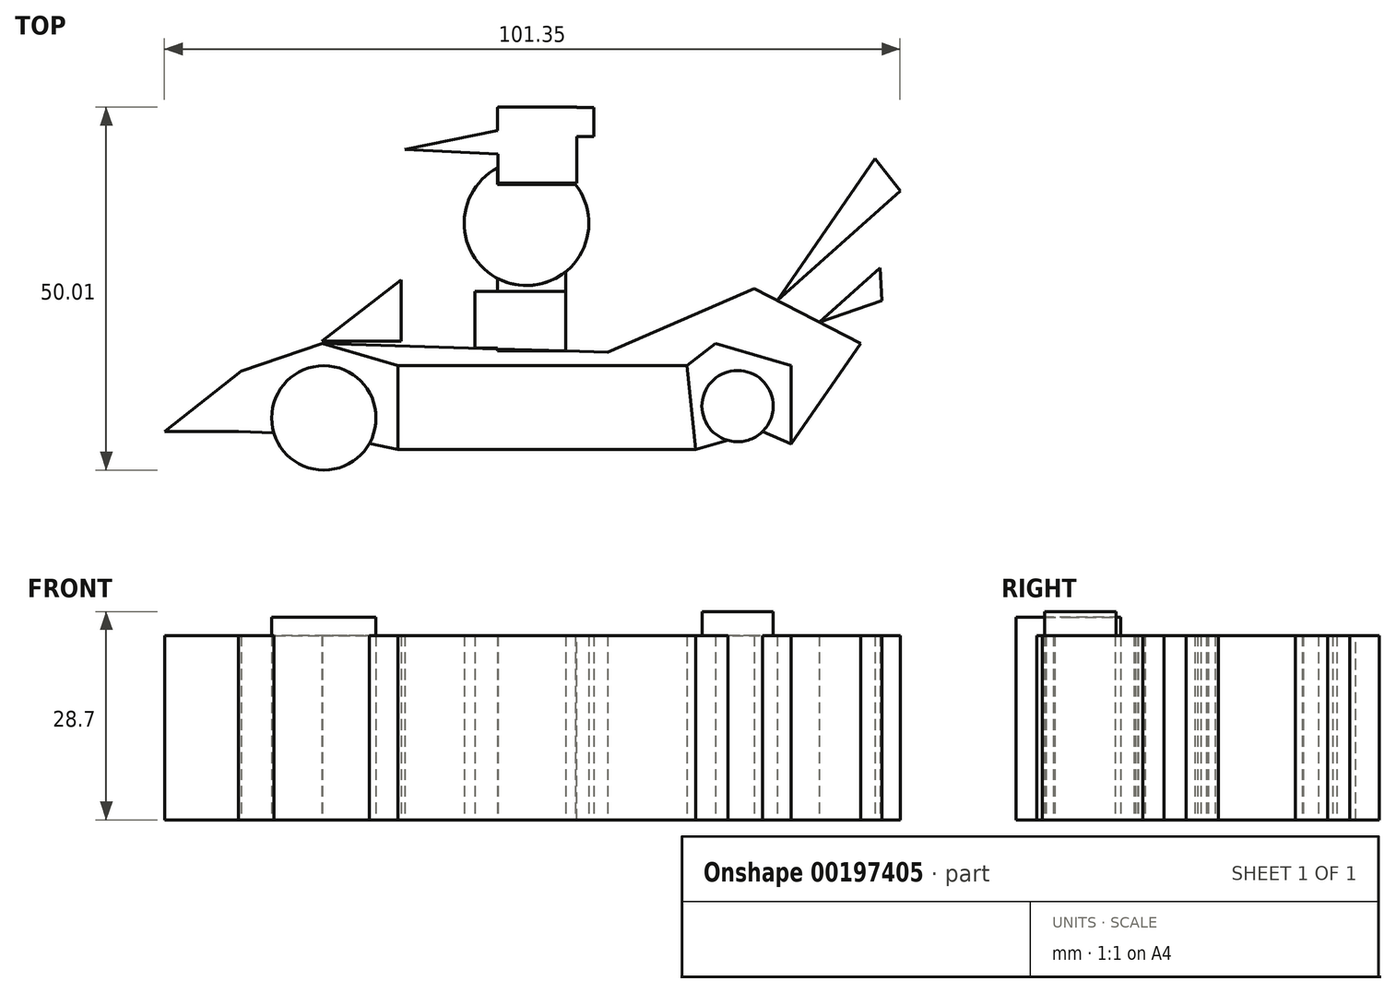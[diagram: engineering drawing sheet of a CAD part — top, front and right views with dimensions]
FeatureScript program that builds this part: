
annotation { "Feature Type Name" : "Feature", "Feature Type Description" : "" }
export const myFeature = defineFeature(function(context is Context, id is Id, definition is map)
    precondition{}
    {
        {
            var Q0;
            Q0=qCreatedBy(makeId("Top.planeOp"),FACE);
            var sketch = newSketch(context, id + "F0", { "sketchPlane" : qUnion([Q0])});
            skLineSegment(sketch, "E0", {"start": v(-28.9, 7.2) * mm, "end": v(10.95, 7.2) * mm});
            skLineSegment(sketch, "E1", {"start": v(-28.9, 7.2) * mm, "end": v(-28.9, -4.36) * mm});
            skLineSegment(sketch, "E2", {"start": v(-28.9, -4.36) * mm, "end": v(12.13, -4.36) * mm});
            skCircle(sketch, "E3", {"center": v(-39.1, 0) * mm, "radius": 7.2 * mm});
            skLineSegment(sketch, "E4", {"start": v(12.13, -4.36) * mm, "end": v(10.95, 7.2) * mm});
            skCircle(sketch, "E5", {"center": v(17.9, 1.63) * mm, "radius": 4.9 * mm});
            skLineSegment(sketch, "E6", {"start": v(-50.45, 6.42) * mm, "end": v(-61.05, -1.86) * mm});
            skLineSegment(sketch, "E7", {"start": v(-61.05, -1.86) * mm, "end": v(-50.84, -1.86) * mm});
            skLineSegment(sketch, "E8", {"start": v(-50.84, -1.86) * mm, "end": v(-50.45, 6.42) * mm});
            skLineSegment(sketch, "E9", {"start": v(-50.45, 6.42) * mm, "end": v(-39.29, 10.27) * mm});
            skLineSegment(sketch, "E10", {"start": v(-39.29, 10.27) * mm, "end": v(-28.9, 7.2) * mm});
            skLineSegment(sketch, "E11", {"start": v(10.95, 7.2) * mm, "end": v(14.89, 10.27) * mm});
            skLineSegment(sketch, "E12", {"start": v(14.89, 10.27) * mm, "end": v(25.28, 7.2) * mm});
            skLineSegment(sketch, "E13", {"start": v(25.28, 7.2) * mm, "end": v(25.28, -3.57) * mm});
            skLineSegment(sketch, "E14", {"start": v(25.28, -3.57) * mm, "end": v(34.85, 10.27) * mm});
            skLineSegment(sketch, "E15", {"start": v(34.85, 10.27) * mm, "end": v(20.22, 17.8) * mm});
            skLineSegment(sketch, "E16", {"start": v(23.35, 16.19) * mm, "end": v(36.85, 35.7) * mm});
            skLineSegment(sketch, "E17", {"start": v(36.85, 35.7) * mm, "end": v(40.3, 31.28) * mm});
            skLineSegment(sketch, "E18", {"start": v(40.3, 31.28) * mm, "end": v(23.35, 16.19) * mm});
            skLineSegment(sketch, "E19", {"start": v(20.22, 17.8) * mm, "end": v(0, 9.06) * mm});
            skLineSegment(sketch, "E20", {"start": v(0, 9.06) * mm, "end": v(-39.29, 10.27) * mm});
            skLineSegment(sketch, "E21", {"start": v(-39.29, 10.27) * mm, "end": v(-28.9, 19.52) * mm});
            skLineSegment(sketch, "E22", {"start": v(-28.9, 19.52) * mm, "end": v(-28.9, 10.27) * mm});
            skLineSegment(sketch, "E23", {"start": v(29.17, 13.2) * mm, "end": v(37.8, 20.88) * mm});
            skLineSegment(sketch, "E24", {"start": v(37.55, 20.88) * mm, "end": v(37.8, 16.19) * mm});
            skCircle(sketch, "E25", {"center": v(-11.17, 26.84) * mm, "radius": 8.59 * mm});
            skLineSegment(sketch, "E26.bottom", {"start": v(-15.38, 36.44) * mm, "end": v(-27.49, 36.44) * mm});
            skLineSegment(sketch, "E26.top", {"start": v(-15.38, 36.05) * mm, "end": v(-27.49, 36.05) * mm});
            skLineSegment(sketch, "E26.left", {"start": v(-15.38, 36.44) * mm, "end": v(-15.38, 36.05) * mm});
            skLineSegment(sketch, "E26.right", {"start": v(-27.49, 36.44) * mm, "end": v(-27.49, 36.05) * mm});
            skLineSegment(sketch, "E27.bottom", {"start": v(-27.49, 36.44) * mm, "end": v(-15.17, 36.44) * mm});
            skLineSegment(sketch, "E27.top", {"start": v(-27.49, 38.75) * mm, "end": v(-15.17, 38.75) * mm});
            skLineSegment(sketch, "E27.left", {"start": v(-27.49, 36.44) * mm, "end": v(-27.49, 38.75) * mm});
            skLineSegment(sketch, "E27.right", {"start": v(-15.17, 36.44) * mm, "end": v(-15.17, 38.75) * mm});
            skLineSegment(sketch, "E28.bottom", {"start": v(-15.17, 38.75) * mm, "end": v(-1.92, 38.75) * mm});
            skLineSegment(sketch, "E28.top", {"start": v(-15.17, 42.79) * mm, "end": v(-1.92, 42.79) * mm});
            skLineSegment(sketch, "E28.left", {"start": v(-15.17, 38.75) * mm, "end": v(-15.17, 42.79) * mm});
            skLineSegment(sketch, "E28.right", {"start": v(-1.92, 38.75) * mm, "end": v(-1.92, 42.79) * mm});
            skLineSegment(sketch, "E29.bottom", {"start": v(-15.17, 36.44) * mm, "end": v(-1.92, 36.44) * mm});
            skLineSegment(sketch, "E29.right", {"start": v(-1.92, 36.44) * mm, "end": v(-1.92, 38.75) * mm});
            skPoint(sketch, "E30.firstSnap0", {"position": v(-15.17, 40.77) * mm});
            skLineSegment(sketch, "E30.bottom", {"start": v(-15.17, 17.41) * mm, "end": v(-18.27, 17.41) * mm});
            skLineSegment(sketch, "E30.top", {"start": v(-15.17, 9.62) * mm, "end": v(-18.27, 9.62) * mm});
            skLineSegment(sketch, "E30.left", {"start": v(-15.17, 17.41) * mm, "end": v(-15.17, 9.62) * mm});
            skLineSegment(sketch, "E30.right", {"start": v(-18.27, 17.41) * mm, "end": v(-18.27, 9.62) * mm});
            skLineSegment(sketch, "E31.bottom", {"start": v(-15.17, 17.41) * mm, "end": v(-5.74, 17.41) * mm});
            skLineSegment(sketch, "E31.top", {"start": v(-15.17, 9.24) * mm, "end": v(-5.74, 9.24) * mm});
            skLineSegment(sketch, "E31.left", {"start": v(-15.17, 17.41) * mm, "end": v(-15.17, 9.24) * mm});
            skLineSegment(sketch, "E31.right", {"start": v(-5.74, 17.41) * mm, "end": v(-5.74, 9.24) * mm});
            skLineSegment(sketch, "E32.top", {"start": v(-15.17, 20.18) * mm, "end": v(-5.74, 20.18) * mm});
            skLineSegment(sketch, "E32.left", {"start": v(-15.17, 17.41) * mm, "end": v(-15.17, 20.18) * mm});
            skLineSegment(sketch, "E32.right", {"start": v(-5.74, 17.41) * mm, "end": v(-5.74, 20.18) * mm});
            skLineSegment(sketch, "E33.bottom", {"start": v(-15.17, 36.44) * mm, "end": v(-4.46, 36.44) * mm});
            skLineSegment(sketch, "E33.top", {"start": v(-15.17, 32.2) * mm, "end": v(-4.46, 32.2) * mm});
            skLineSegment(sketch, "E33.left", {"start": v(-15.17, 36.44) * mm, "end": v(-15.17, 32.2) * mm});
            skLineSegment(sketch, "E33.right", {"start": v(-4.46, 36.44) * mm, "end": v(-4.46, 32.2) * mm});
            skLineSegment(sketch, "E34", {"start": v(-50.84, -1.86) * mm, "end": v(-45.97, -2.1) * mm});
            skLineSegment(sketch, "E35", {"start": v(-32.8, -3.5) * mm, "end": v(-28.9, -4.36) * mm});
            skLineSegment(sketch, "E36", {"start": v(12.13, -4.36) * mm, "end": v(16.55, -3.1) * mm});
            skLineSegment(sketch, "E37", {"start": v(21.36, -1.86) * mm, "end": v(25.28, -3.57) * mm});
            skLineSegment(sketch, "E38", {"start": v(29.17, 13.2) * mm, "end": v(37.8, 16.19) * mm});
            skSolve(sketch);
        }
        {
            var Q0;
            Q0=makeQuery(id+"F0.imprint","IMPRINT",FACE,{"disambiguationData":[TD([[makeQuery(id+"F0.imprint","IMPRINT",EDGE,{"derivedFrom":sQuery(id+"F0.wireOp",EDGE,"E0")}),-1.0]])]});
            extrude(context, id + "F1", {"entities" : qUnion([Q0]), "depth" : 25.4 * mm});
        }
        {
            var Q0;
            {var subQ0=sQuery(id+"F0.wireOp",EDGE,"E3");var subQ1=makeQuery(id+"F0.imprint","INTERSECT",VERTEX,{"derivedFrom":[subQ0,sQuery(id+"F0.wireOp",EDGE,"E34")]});Q0=makeQuery(id+"F0.imprint","IMPRINT",FACE,{"disambiguationData":[TD([[makeQuery(id+"F0.imprint","IMPRINT",EDGE,{"disambiguationData":[TD([[subQ1,-1.0]])],"derivedFrom":subQ0}),1.0]])]});}
            extrude(context, id + "F2", {"entities" : qUnion([Q0]), "depth" : 27.94 * mm});
        }
        {
            var Q0;
            Q0=makeQuery(id+"F0.imprint","IMPRINT",FACE,{"disambiguationData":[TD([[makeQuery(id+"F0.imprint","IMPRINT",EDGE,{"derivedFrom":sQuery(id+"F0.wireOp",EDGE,"E1")}),-1.0]])]});
            extrude(context, id + "F3", {"entities" : qUnion([Q0]), "depth" : 25.4 * mm});
        }
        {
            var Q0;
            Q0=makeQuery(id+"F0.imprint","IMPRINT",FACE,{"disambiguationData":[TD([[makeQuery(id+"F0.imprint","IMPRINT",EDGE,{"derivedFrom":sQuery(id+"F0.wireOp",EDGE,"E6")}),1.0]])]});
            extrude(context, id + "F4", {"entities" : qUnion([Q0]), "operationType" : NewBodyOperationType.ADD, "depth" : 25.4 * mm});
        }
        {
            var Q0;
            Q0=makeQuery(id+"F0.imprint","IMPRINT",FACE,{"disambiguationData":[TD([[makeQuery(id+"F0.imprint","IMPRINT",EDGE,{"derivedFrom":sQuery(id+"F0.wireOp",EDGE,"E0")}),1.0]])]});
            extrude(context, id + "F5", {"entities" : qUnion([Q0]), "depth" : 25.4 * mm});
        }
        {
            var Q0;
            {var subQ0=sQuery(id+"F0.wireOp",EDGE,"E31.right");Q0=makeQuery(id+"F0.imprint","IMPRINT",FACE,{"disambiguationData":[TD([[makeQuery(id+"F0.imprint","IMPRINT",EDGE,{"derivedFrom":subQ0}),-1.0]])]});}
            extrude(context, id + "F6", {"entities" : qUnion([Q0]), "depth" : 25.4 * mm});
        }
        {
            var Q0;
            {var subQ0=sQuery(id+"F0.wireOp",EDGE,"E30.bottom");Q0=makeQuery(id+"F0.imprint","IMPRINT",FACE,{"disambiguationData":[TD([[makeQuery(id+"F0.imprint","IMPRINT",EDGE,{"derivedFrom":subQ0}),1.0]])]});}
            extrude(context, id + "F7", {"entities" : qUnion([Q0]), "operationType" : NewBodyOperationType.ADD, "depth" : 25.4 * mm});
        }
        {
            var Q0;
            {var subQ1=sQuery(id+"F0.wireOp",EDGE,"E32.top");Q0=makeQuery(id+"F0.imprint","IMPRINT",FACE,{"disambiguationData":[TD([[makeQuery(id+"F0.imprint","IMPRINT",EDGE,{"derivedFrom":subQ1}),1.0]])]});}
            extrude(context, id + "F8", {"entities" : qUnion([Q0]), "depth" : 25.4 * mm});
        }
        {
            var Q0;
            {var subQ0=sQuery(id+"F0.wireOp",EDGE,"E5");var subQ1=makeQuery(id+"F0.imprint","INTERSECT",VERTEX,{"derivedFrom":[subQ0,sQuery(id+"F0.wireOp",EDGE,"E36")]});Q0=makeQuery(id+"F0.imprint","IMPRINT",FACE,{"disambiguationData":[TD([[makeQuery(id+"F0.imprint","IMPRINT",EDGE,{"disambiguationData":[TD([[subQ1,-1.0]])],"derivedFrom":subQ0}),1.0]])]});}
            extrude(context, id + "F9", {"entities" : qUnion([Q0]), "depth" : 25.4 * mm});
        }
        {
            var Q0;
            {var subQ4=sQuery(id+"F0.wireOp",EDGE,"E31.bottom");Q0=makeQuery(id+"F0.imprint","IMPRINT",FACE,{"disambiguationData":[TD([[makeQuery(id+"F0.imprint","IMPRINT",EDGE,{"derivedFrom":subQ4}),1.0]])]});}
            var sketch = newSketch(context, id + "F10", { "sketchPlane" : qUnion([Q0])});
            skLineSegment(sketch, "E39", {"start": v(-28.42, 19) * mm, "end": v(-28.42, 10.56) * mm});
            skLineSegment(sketch, "E40", {"start": v(-28.42, 10.56) * mm, "end": v(-39.35, 10.56) * mm});
            skLineSegment(sketch, "E41", {"start": v(-39.35, 10.56) * mm, "end": v(-28.42, 19) * mm});
            skSolve(sketch);
        }
        {
            var Q0;
            Q0=makeQuery(id+"F10.imprint","IMPRINT",FACE,{"disambiguationData":[TD([[makeQuery(id+"F10.imprint","IMPRINT",EDGE,{"derivedFrom":sQuery(id+"F10.wireOp",EDGE,"E39")}),-1.0]])]});
            extrude(context, id + "F11", {"entities" : qUnion([Q0]), "depth" : 25.4 * mm});
        }
        {
            var Q0;
            Q0=qCreatedBy(makeId("Top.planeOp"),FACE);
            var sketch = newSketch(context, id + "F12", { "sketchPlane" : qUnion([Q0])});
            skLineSegment(sketch, "E42", {"start": v(-15.08, 19.5) * mm, "end": v(-5.63, 19.5) * mm});
            skLineSegment(sketch, "E43", {"start": v(-5.63, 19.5) * mm, "end": v(-5.63, 17.09) * mm});
            skLineSegment(sketch, "E44", {"start": v(-5.63, 17.09) * mm, "end": v(-15.08, 17.09) * mm});
            skLineSegment(sketch, "E45", {"start": v(-15.08, 17.09) * mm, "end": v(-15.08, 19.5) * mm});
            skLineSegment(sketch, "E46", {"start": v(-15.08, 36.39) * mm, "end": v(-15.08, 32.37) * mm});
            skLineSegment(sketch, "E47", {"start": v(-15.08, 32.37) * mm, "end": v(-4.22, 32.37) * mm});
            skLineSegment(sketch, "E48", {"start": v(-4.22, 32.37) * mm, "end": v(-4.22, 42.82) * mm});
            skLineSegment(sketch, "E49", {"start": v(-4.22, 42.82) * mm, "end": v(-15.08, 42.82) * mm});
            skLineSegment(sketch, "E50", {"start": v(-15.08, 42.82) * mm, "end": v(-15.08, 39.6) * mm});
            skLineSegment(sketch, "E51", {"start": v(-15.08, 39.6) * mm, "end": v(-27.94, 36.99) * mm});
            skLineSegment(sketch, "E52", {"start": v(-27.94, 36.99) * mm, "end": v(-15.08, 36.39) * mm});
            skSolve(sketch);
        }
        {
            var Q0;
            Q0=makeQuery(id+"F0.imprint","IMPRINT",FACE,{"disambiguationData":[TD([[makeQuery(id+"F0.imprint","IMPRINT",EDGE,{"derivedFrom":sQuery(id+"F0.wireOp",EDGE,"E28.top")}),-1.0]])]});
            extrude(context, id + "F13", {"entities" : qUnion([Q0]), "depth" : 25.4 * mm});
        }
        {
            var Q0;
            Q0=makeQuery(id+"F12.imprint","IMPRINT",FACE,{"disambiguationData":[TD([[makeQuery(id+"F12.imprint","IMPRINT",EDGE,{"derivedFrom":sQuery(id+"F12.wireOp",EDGE,"E46")}),1.0]])]});
            extrude(context, id + "F14", {"entities" : qUnion([Q0]), "operationType" : NewBodyOperationType.ADD, "depth" : 25.4 * mm});
        }
        {
            var Q0;
            Q0=makeQuery(id+"F0.imprint","IMPRINT",FACE,{"disambiguationData":[TD([[makeQuery(id+"F0.imprint","IMPRINT",EDGE,{"derivedFrom":sQuery(id+"F0.wireOp",EDGE,"E4")}),-1.0]])]});
            extrude(context, id + "F15", {"entities" : qUnion([Q0]), "depth" : 25.4 * mm});
        }
        {
            var Q0;
            Q0=makeQuery(id+"F0.imprint","IMPRINT",FACE,{"disambiguationData":[TD([[makeQuery(id+"F0.imprint","IMPRINT",EDGE,{"derivedFrom":sQuery(id+"F0.wireOp",EDGE,"E16")}),-1.0]])]});
            extrude(context, id + "F16", {"entities" : qUnion([Q0]), "depth" : 25.4 * mm});
        }
        {
            var Q0;
            {var subQ0=sQuery(id+"F0.wireOp",EDGE,"E38");Q0=makeQuery(id+"F0.imprint","IMPRINT",FACE,{"disambiguationData":[TD([[makeQuery(id+"F0.imprint","IMPRINT",EDGE,{"derivedFrom":subQ0}),1.0]])]});}
            extrude(context, id + "F17", {"entities" : qUnion([Q0]), "depth" : 25.4 * mm});
        }
        {
            var Q0;
            {var subQ4=sQuery(id+"F0.wireOp",EDGE,"E31.bottom");Q0=makeQuery(id+"F0.imprint","IMPRINT",FACE,{"disambiguationData":[TD([[makeQuery(id+"F0.imprint","IMPRINT",EDGE,{"derivedFrom":subQ4}),1.0]])]});}
            var sketch = newSketch(context, id + "F18", { "sketchPlane" : qUnion([Q0])});
            skSolve(sketch);
        }
        {
            var Q0;
            {var subQ0=sQuery(id+"F0.wireOp",EDGE,"E32.top");Q0=makeQuery(id+"F0.imprint","IMPRINT",FACE,{"disambiguationData":[TD([[makeQuery(id+"F0.imprint","IMPRINT",EDGE,{"derivedFrom":subQ0}),-1.0]])]});}
            extrude(context, id + "F19", {"entities" : qUnion([Q0]), "operationType" : NewBodyOperationType.ADD, "depth" : 25.4 * mm});
        }
        {
            var Q0;
            {var subQ4=sQuery(id+"F0.wireOp",EDGE,"E31.bottom");Q0=makeQuery(id+"F18.imprint","IMPRINT",FACE,{"disambiguationData":[TD([[makeQuery(id+"F18.imprint","IMPRINT",EDGE,{"derivedFrom":makeQuery(id+"F0.imprint","IMPRINT",EDGE,{"derivedFrom":subQ4})}),1.0]])]});}
            extrude(context, id + "F20", {"entities" : qUnion([Q0]), "depth" : 25.4 * mm});
        }
        {
            var Q0;
            Q0=makeQuery(id+"F9.opExtrude","CAP_FACE",FACE,{"disambiguationData":[OSD([sQuery(id+"F0.wireOp",EDGE,"E5")])],"isStart":false});
            extrude(context, id + "F21", {"entities" : qUnion([Q0]), "operationType" : NewBodyOperationType.ADD, "depth" : 3.3 * mm});
        }
    });
